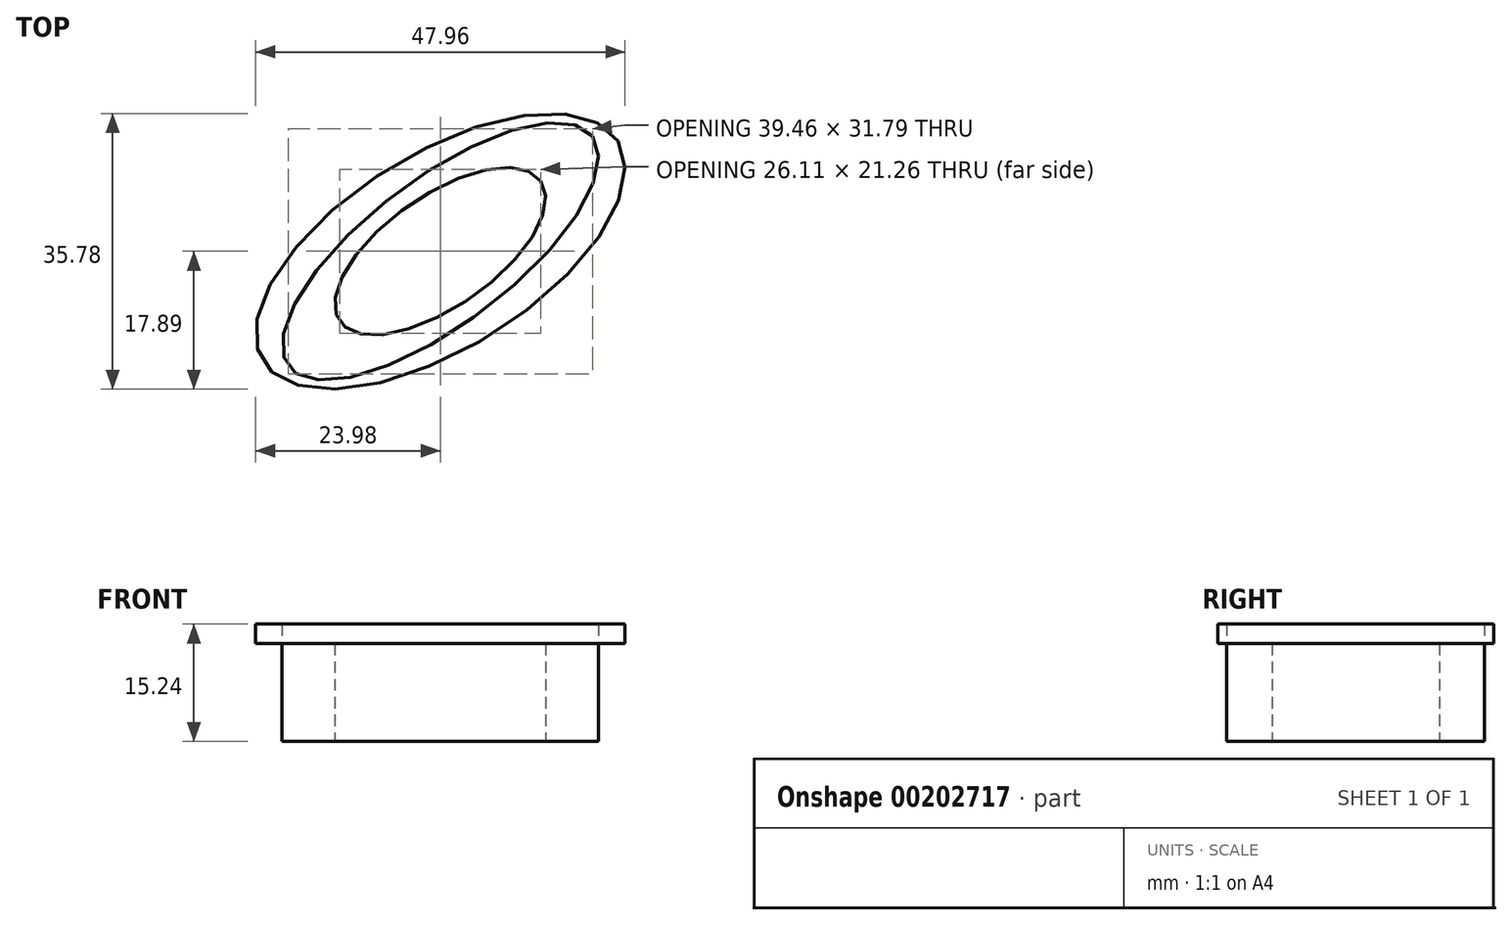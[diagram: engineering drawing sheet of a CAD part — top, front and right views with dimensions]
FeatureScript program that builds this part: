
annotation { "Feature Type Name" : "Feature", "Feature Type Description" : "" }
export const myFeature = defineFeature(function(context is Context, id is Id, definition is map)
    precondition{}
    {
        {
            var Q0;
            Q0=qCreatedBy(makeId("Top.planeOp"),FACE);
            var sketch = newSketch(context, id + "F0", { "sketchPlane" : qUnion([Q0])});
            skEllipse(sketch, "E0", {"center": v(0, 0) * mm, "majorRadius": 24.75 * mm, "minorRadius": 9.46 * mm, "majorAxis": v(0.8, 0.6)});
            skSolve(sketch);
        }
        {
            var Q0;
            Q0=makeQuery(id+"F0.imprint","IMPRINT",FACE,{"disambiguationData":[TD([[makeQuery(id+"F0.imprint","IMPRINT",EDGE,{"derivedFrom":sQuery(id+"F0.wireOp",EDGE,"E0")}),1.0]])]});
            extrude(context, id + "F1", {"entities" : qUnion([Q0]), "depth" : 12.7 * mm});
        }
        {
            var Q0;
            Q0=makeQuery(id+"F1.opExtrude","CAP_FACE",FACE,{"disambiguationData":[OSD([sQuery(id+"F0.wireOp",EDGE,"E0")])],"isStart":false});
            var sketch = newSketch(context, id + "F2", { "sketchPlane" : qUnion([Q0])});
            skEllipse(sketch, "E1", {"center": v(0, 0) * mm, "majorRadius": 15.92 * mm, "minorRadius": 7.23 * mm, "majorAxis": v(0.82, 0.57)});
            skSolve(sketch);
        }
        {
            var Q0;
            Q0=makeQuery(id+"F2.imprint","IMPRINT",FACE,{"disambiguationData":[TD([[makeQuery(id+"F2.imprint","IMPRINT",EDGE,{"derivedFrom":sQuery(id+"F2.wireOp",EDGE,"E1")}),1.0]])]});
            extrude(context, id + "F3", {"entities" : qUnion([Q0]), "operationType" : NewBodyOperationType.REMOVE, "oppositeDirection" : true, "depth" : 25.4 * mm});
        }
        {
            var Q0;
            Q0=makeQuery(id+"F1.opExtrude","CAP_FACE",FACE,{"disambiguationData":[OSD([sQuery(id+"F0.wireOp",EDGE,"E0")])],"isStart":false});
            var sketch = newSketch(context, id + "F4", { "sketchPlane" : qUnion([Q0])});
            skEllipse(sketch, "E2", {"center": v(0, 0) * mm, "majorRadius": 27.1 * mm, "minorRadius": 12.66 * mm, "majorAxis": v(0.85, 0.53)});
            skSolve(sketch);
        }
        {
            var Q0;
            Q0=makeQuery(id+"F4.imprint","IMPRINT",FACE,{"disambiguationData":[TD([[makeQuery(id+"F4.imprint","IMPRINT",EDGE,{"derivedFrom":sQuery(id+"F4.wireOp",EDGE,"E2")}),1.0]])]});
            extrude(context, id + "F5", {"entities" : qUnion([Q0]), "depth" : 2.54 * mm});
        }
    });
